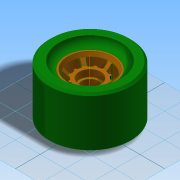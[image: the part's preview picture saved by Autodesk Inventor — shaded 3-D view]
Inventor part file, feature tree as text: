
AUTODESK INVENTOR PART (.ipt)
format: ipt  version: 2015 (Build 190159000, 159)  size: 414,208 bytes
history: native  units: in
note: dims shown in document units (in); Inventor stores cm internally (conversion verified against a paired STEP export)
features: extrude x4, chamfer x4, sketch x3, fillet x3, pattern_circular x2, revolve x1
ambient origin geometry x8: Origin, YZ Plane, XZ Plane, XY Plane, X Axis, Y Axis, Z Axis, Center Point
bodies: Solid1 (feature_tree)
feature tree (17):
  revolve  "Revolution1"  [1 undecoded]
  sketch  "Sketch3"  dims[d4=0.44in d6=0.815in]
  extrude  "Bearing Holder"  Depth=0.815in
  extrude  "Bearing Holder Lip"  Depth=0.02in
  extrude  "Spoke"  Depth=0.02in
  chamfer  "Chamfer1"  Distance=0.36in
  chamfer  "Chamfer2"  Angle=90.0deg  [1 undecoded]
  fillet  "Fillet1"  Radius=1.14in
  pattern_circular  "Spoke Pattern"  [2 undecoded]
  extrude  "Nib"  Depth=0.02in
  fillet  "Fillet2"  Radius=0.1in
  fillet  "Fillet3"  Radius=0.296in
  pattern_circular  "Nib Pattern"  [2 undecoded]
  chamfer  "Wheel Inner Chamfer"  Distance=0.296in
  chamfer  "Wheel Outer Chamfer"  Distance=0.168in Angle=45.0deg
  sketch  "Sketch2"  dims[d0=1.63in d2=0.38in]
  sketch  "Sketch5"  dims[d7=0.29in d9=1.025in d10=0.2898in d11=0.36in d12=90.0deg d13=1.14in d14=0.834in d15=0.0in d17=0.865in d18=0.1in d19=0.296in d20=0.0in d21=0.15in d22=0.296in d23=0.0in d24=0.168in d25=0.18in d26=45.0deg d27=0.05in d28=2.3622in d29=360.0deg d31=0.168in d32=0.18in d33=45.0deg d34=30.0deg d35=0.09in d36=0.06in d37=0.296in d38=0.0in d39=0.05in d40=0.02in d41=2.3622in d42=360.0deg d44=0.08in d45=0.18in d46=45.0deg d47=0.08in d48=0.292in d49=45.0deg]
note: 6 required parameter values undecoded (feature->parameter linkage not recoverable at this tier; creation-order binding heuristic only, values carry confidence <= 0.55)